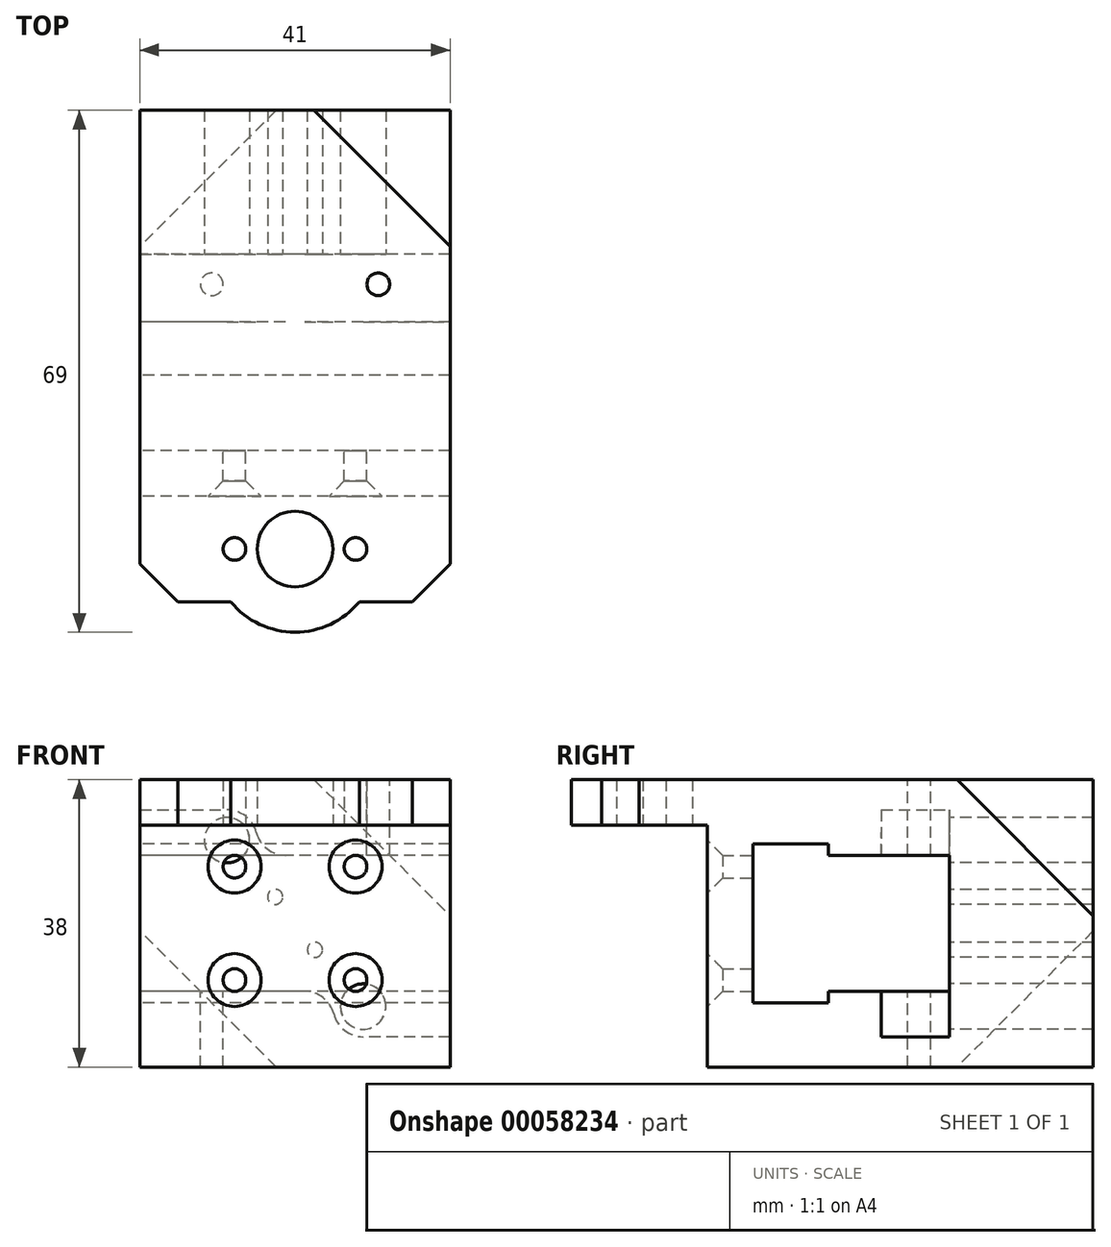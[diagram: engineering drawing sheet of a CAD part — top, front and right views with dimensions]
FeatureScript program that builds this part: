
annotation { "Feature Type Name" : "Feature", "Feature Type Description" : "" }
export const myFeature = defineFeature(function(context is Context, id is Id, definition is map)
    precondition{}
    {
        {
            var Q0;
            Q0=qCreatedBy(makeId("Right.planeOp"),FACE);
            var sketch = newSketch(context, id + "F0", { "sketchPlane" : qUnion([Q0])});
            skLineSegment(sketch, "E0", {"start": v(0, 0) * mm, "end": v(22, 0) * mm, "construction": true});
            skLineSegment(sketch, "E1", {"start": v(22, 0) * mm, "end": v(22, 31.5) * mm, "construction": true});
            skLineSegment(sketch, "E2", {"start": v(0, 10.5) * mm, "end": v(10, 10.5) * mm});
            skLineSegment(sketch, "E3", {"start": v(10, 10.5) * mm, "end": v(10, 9) * mm});
            skLineSegment(sketch, "E4", {"start": v(10, 9) * mm, "end": v(26, 9) * mm});
            skLineSegment(sketch, "E5.MirrorCS", {"start": v(0, -10.5) * mm, "end": v(10, -10.5) * mm});
            skLineSegment(sketch, "E6.MirrorCS", {"start": v(10, -10.5) * mm, "end": v(10, -9) * mm});
            skLineSegment(sketch, "E7.MirrorCS", {"start": v(10, -9) * mm, "end": v(26, -9) * mm});
            skLineSegment(sketch, "E8", {"start": v(0, 10.5) * mm, "end": v(0, -10.5) * mm});
            skLineSegment(sketch, "E9", {"start": v(26, 9) * mm, "end": v(26, 19) * mm});
            skLineSegment(sketch, "E10", {"start": v(26, 19) * mm, "end": v(-20, 19) * mm});
            skLineSegment(sketch, "E11", {"start": v(-20, 19) * mm, "end": v(-20, 13) * mm});
            skLineSegment(sketch, "E12", {"start": v(-20, 13) * mm, "end": v(-6, 13) * mm});
            skLineSegment(sketch, "E13", {"start": v(-6, 13) * mm, "end": v(-6, -19) * mm});
            skLineSegment(sketch, "E14.MirrorCS", {"start": v(26, -9) * mm, "end": v(26, -19) * mm});
            skLineSegment(sketch, "E15", {"start": v(26, -19) * mm, "end": v(-6, -19) * mm});
            skSolve(sketch);
        }
        {
            var Q0;
            Q0 = qSketchRegion(id + "F0", true);
            extrude(context, id + "F1", {"entities" : qUnion([Q0]), "depth" : 41 * mm, "symmetric" : true});
        }
        {
            var Q0;
            Q0=makeQuery(id+"F1.opExtrude","SWEPT_FACE",FACE,{"disambiguationData":[OSD([sQuery(id+"F0.wireOp",EDGE,"E12")])]});
            var sketch = newSketch(context, id + "F2", { "sketchPlane" : qUnion([Q0])});
            skLineSegment(sketch, "E16", {"start": v(-20.5, 13) * mm, "end": v(20.5, 13) * mm, "construction": true});
            skLineSegment(sketch, "E17", {"start": v(0, 13) * mm, "end": v(0, 20) * mm, "construction": true});
            skCircle(sketch, "E18", {"center": v(-8, 13) * mm, "radius": 1.5 * mm});
            skCircle(sketch, "E19.MirrorC", {"center": v(8, 13) * mm, "radius": 1.5 * mm});
            skCircle(sketch, "E20", {"center": v(0, 13) * mm, "radius": 5 * mm});
            skSolve(sketch);
        }
        {
            var Q0;
            Q0 = qSketchRegion(id + "F2", true);
            extrude(context, id + "F3", {"entities" : qUnion([Q0]), "operationType" : NewBodyOperationType.REMOVE, "endBound" : BoundingType.THROUGH_ALL, "oppositeDirection" : true, "depth" : 25 * mm});
        }
        {
            var Q0;
            Q0=makeQuery(id+"F1.opExtrude","SWEPT_FACE",FACE,{"disambiguationData":[OSD([sQuery(id+"F0.wireOp",EDGE,"E10")])]});
            var sketch = newSketch(context, id + "F4", { "sketchPlane" : qUnion([Q0])});
            skArc(sketch, "E21", {"start": v(8.49, -20) * mm, "mid": v(0, -24) * mm, "end": v(-8.49, -20) * mm});
            skLineSegment(sketch, "E22", {"start": v(8.49, -20) * mm, "end": v(-8.49, -20) * mm});
            skSolve(sketch);
        }
        {
            var Q0;
            Q0 = qSketchRegion(id + "F4", true);
            var Q1;
            Q1=makeQuery(id+"F1.opExtrude","SWEPT_FACE",FACE,{"disambiguationData":[OSD([sQuery(id+"F0.wireOp",EDGE,"E12")])]});
            extrude(context, id + "F5", {"entities" : qUnion([Q0]), "operationType" : NewBodyOperationType.ADD, "endBound" : BoundingType.UP_TO_SURFACE, "oppositeDirection" : true, "endBoundEntityFace" : qUnion([Q1]), "depth" : 25 * mm});
        }
        {
            var Q0;
            Q0=makeQuery(id+"F1.opExtrude","SWEPT_FACE",FACE,{"disambiguationData":[OSD([sQuery(id+"F0.wireOp",EDGE,"E8")])]});
            var sketch = newSketch(context, id + "F6", { "sketchPlane" : qUnion([Q0])});
            skLineSegment(sketch, "E23", {"start": v(-20.5, 0) * mm, "end": v(0, 0) * mm, "construction": true});
            skLineSegment(sketch, "E24", {"start": v(0, 0) * mm, "end": v(0, 10.5) * mm, "construction": true});
            skCircle(sketch, "E25", {"center": v(-8, 7.5) * mm, "radius": 1.5 * mm});
            skCircle(sketch, "E26.MirrorC", {"center": v(8, 7.5) * mm, "radius": 1.5 * mm});
            skCircle(sketch, "E27.MirrorC", {"center": v(8, -7.5) * mm, "radius": 1.5 * mm});
            skCircle(sketch, "E28.MirrorC", {"center": v(-8, -7.5) * mm, "radius": 1.5 * mm});
            skSolve(sketch);
        }
        {
            var Q0;
            Q0 = qSketchRegion(id + "F6", true);
            extrude(context, id + "F7", {"entities" : qUnion([Q0]), "operationType" : NewBodyOperationType.REMOVE, "endBound" : BoundingType.THROUGH_ALL, "oppositeDirection" : true, "depth" : 25 * mm});
        }
        {
            var Q0;
            Q0=makeQuery(id+"F7.boolean.opBoolean","INTERSECT",EDGE,{"derivedFrom":[makeQuery(id+"F1.opExtrude","SWEPT_FACE",FACE,{"disambiguationData":[OSD([sQuery(id+"F0.wireOp",EDGE,"E13")])]}),makeQuery(id+"F7.opExtrude","SWEPT_FACE",FACE,{"disambiguationData":[OSD([sQuery(id+"F6.wireOp",EDGE,"E26.MirrorC")])]})]});
            var Q1;
            Q1=makeQuery(id+"F7.boolean.opBoolean","INTERSECT",EDGE,{"derivedFrom":[makeQuery(id+"F1.opExtrude","SWEPT_FACE",FACE,{"disambiguationData":[OSD([sQuery(id+"F0.wireOp",EDGE,"E13")])]}),makeQuery(id+"F7.opExtrude","SWEPT_FACE",FACE,{"disambiguationData":[OSD([sQuery(id+"F6.wireOp",EDGE,"E25")])]})]});
            var Q2;
            Q2=makeQuery(id+"F7.boolean.opBoolean","INTERSECT",EDGE,{"derivedFrom":[makeQuery(id+"F1.opExtrude","SWEPT_FACE",FACE,{"disambiguationData":[OSD([sQuery(id+"F0.wireOp",EDGE,"E13")])]}),makeQuery(id+"F7.opExtrude","SWEPT_FACE",FACE,{"disambiguationData":[OSD([sQuery(id+"F6.wireOp",EDGE,"E28.MirrorC")])]})]});
            var Q3;
            Q3=makeQuery(id+"F7.boolean.opBoolean","INTERSECT",EDGE,{"derivedFrom":[makeQuery(id+"F1.opExtrude","SWEPT_FACE",FACE,{"disambiguationData":[OSD([sQuery(id+"F0.wireOp",EDGE,"E13")])]}),makeQuery(id+"F7.opExtrude","SWEPT_FACE",FACE,{"disambiguationData":[OSD([sQuery(id+"F6.wireOp",EDGE,"E27.MirrorC")])]})]});
            chamfer(context, id + "F8", {"entities" : qUnion([Q0, Q1, Q2, Q3]), "width" : 2 * mm, "tangentPropagation" : true});
        }
        {
            var Q0;
            Q0=makeQuery(id+"F5.boolean.opBoolean","MERGE",FACE,{"derivedFrom":[makeQuery(id+"F1.opExtrude","SWEPT_FACE",FACE,{"disambiguationData":[OSD([sQuery(id+"F0.wireOp",EDGE,"E10")])]}),makeQuery(id+"F5.opExtrude","CAP_FACE",FACE,{"disambiguationData":[OSD([sQuery(id+"F4.wireOp",EDGE,"E21"),sQuery(id+"F4.wireOp",EDGE,"E22")])],"isStart":true})]});
            var sketch = newSketch(context, id + "F9", { "sketchPlane" : qUnion([Q0])});
            skLineSegment(sketch, "E29", {"start": v(20.5, 22) * mm, "end": v(-20.5, 22) * mm, "construction": true});
            skLineSegment(sketch, "E30", {"start": v(0, 22) * mm, "end": v(0, 0) * mm, "construction": true});
            skCircle(sketch, "E31", {"center": v(-11, 22) * mm, "radius": 1.5 * mm});
            skCircle(sketch, "E32.MirrorC", {"center": v(11, 22) * mm, "radius": 1.5 * mm});
            skSolve(sketch);
        }
        {
            var Q0;
            Q0 = qSketchRegion(id + "F9", true);
            extrude(context, id + "F10", {"entities" : qUnion([Q0]), "operationType" : NewBodyOperationType.REMOVE, "endBound" : BoundingType.THROUGH_ALL, "oppositeDirection" : true, "depth" : 25 * mm});
        }
        {
            var Q0;
            Q0=makeQuery(id+"F1.opExtrude","SWEPT_FACE",FACE,{"disambiguationData":[OSD([sQuery(id+"F0.wireOp",EDGE,"E9")])]});
            var sketch = newSketch(context, id + "F11", { "sketchPlane" : qUnion([Q0])});
            skLineSegment(sketch, "E33.0", {"start": v(9.5, 19) * mm, "end": v(12.5, 19) * mm, "construction": true});
            skLineSegment(sketch, "E34", {"start": v(11, 11) * mm, "end": v(11, 19) * mm, "construction": true});
            skCircle(sketch, "E35", {"center": v(2.63, 3.5) * mm, "radius": 1 * mm});
            skLineSegment(sketch, "E36", {"start": v(11, 11) * mm, "end": v(9, 11) * mm, "construction": true});
            skCircle(sketch, "E37", {"center": v(9, 11) * mm, "radius": 2 * mm, "construction": true});
            skCircle(sketch, "E38", {"center": v(9, 11) * mm, "radius": 3 * mm});
            skLineSegment(sketch, "E39", {"start": v(0, 9) * mm, "end": v(0, 0) * mm, "construction": true});
            skLineSegment(sketch, "E40", {"start": v(0, 0) * mm, "end": v(-37.44, 0) * mm, "construction": true});
            skLineSegment(sketch, "E41.bottom", {"start": v(-20.5, 19) * mm, "end": v(20.5, 19) * mm});
            skLineSegment(sketch, "E41.top", {"start": v(-20.5, -19) * mm, "end": v(20.5, -19) * mm});
            skLineSegment(sketch, "E41.left", {"start": v(-20.5, 19) * mm, "end": v(-20.5, -19) * mm});
            skLineSegment(sketch, "E41.right", {"start": v(20.5, 19) * mm, "end": v(20.5, -19) * mm});
            skCircle(sketch, "E42.MirrorC", {"center": v(-2.63, 3.5) * mm, "radius": 1 * mm, "construction": true});
            skCircle(sketch, "E43.MirrorC", {"center": v(-9, 11) * mm, "radius": 3 * mm, "construction": true});
            skCircle(sketch, "E44.MirrorC", {"center": v(-2.63, -3.5) * mm, "radius": 1 * mm});
            skCircle(sketch, "E45.MirrorC", {"center": v(-9, -11) * mm, "radius": 3 * mm});
            skSolve(sketch);
        }
        {
            var Q0;
            Q0 = qSketchRegion(id + "F11", true);
            extrude(context, id + "F12", {"entities" : qUnion([Q0]), "operationType" : NewBodyOperationType.ADD, "depth" : 19 * mm});
        }
        {
            var Q0;
            Q0=makeQuery(id+"F12.opExtrude","CAP_FACE",FACE,{"disambiguationData":[OSD([sQuery(id+"F11.wireOp",EDGE,"E35"),sQuery(id+"F11.wireOp",EDGE,"E38"),sQuery(id+"F11.wireOp",EDGE,"E41.bottom"),sQuery(id+"F11.wireOp",EDGE,"E41.top"),sQuery(id+"F11.wireOp",EDGE,"E41.left"),sQuery(id+"F11.wireOp",EDGE,"E41.right"),sQuery(id+"F11.wireOp",EDGE,"E44.MirrorC"),sQuery(id+"F11.wireOp",EDGE,"E45.MirrorC")])],"isStart":false});
            var sketch = newSketch(context, id + "F13", { "sketchPlane" : qUnion([Q0])});
            skCircle(sketch, "E46.0", {"center": v(9, 11) * mm, "radius": 3 * mm});
            skCircle(sketch, "E46.1", {"center": v(-9, -11) * mm, "radius": 3 * mm});
            skSolve(sketch);
        }
        {
            var Q0;
            Q0 = qSketchRegion(id + "F13", true);
            var Q1;
            Q1=makeQuery(id+"F10.boolean.opBoolean","COPY",FACE,{"disambiguationData":[TD([makeQuery(id+"F1.opExtrude","SWEPT_FACE",FACE,{"disambiguationData":[OSD([sQuery(id+"F0.wireOp",EDGE,"E4")])]})])],"derivedFrom":makeQuery(id+"F10.opExtrude","SWEPT_FACE",FACE,{"disambiguationData":[OSD([sQuery(id+"F9.wireOp",EDGE,"E31")])]})});
            extrude(context, id + "F14", {"entities" : qUnion([Q0]), "operationType" : NewBodyOperationType.REMOVE, "oppositeDirection" : true, "endBoundEntityFace" : qUnion([Q1]), "depth" : 28 * mm});
        }
        {
            var Q0;
            Q0=makeQuery(id+"F14.boolean.opBoolean","COPY",FACE,{"derivedFrom":makeQuery(id+"F14.opExtrude","CAP_FACE",FACE,{"disambiguationData":[OSD([sQuery(id+"F13.wireOp",EDGE,"E46.0")])],"isStart":false})});
            var sketch = newSketch(context, id + "F15", { "sketchPlane" : qUnion([Q0])});
            skArc(sketch, "E47.0", {"start": v(11.24, 9) * mm, "mid": v(9, 14) * mm, "end": v(6.76, 9) * mm});
            skLineSegment(sketch, "E48.0", {"start": v(20.5, -19) * mm, "end": v(20.5, 19) * mm, "construction": true});
            skLineSegment(sketch, "E49", {"start": v(11.24, 9) * mm, "end": v(20.5, 9) * mm});
            skLineSegment(sketch, "E50", {"start": v(20.5, 9) * mm, "end": v(20.5, 19) * mm});
            skLineSegment(sketch, "E51", {"start": v(20.5, 19) * mm, "end": v(0, 19) * mm});
            skLineSegment(sketch, "E52", {"start": v(0, 19) * mm, "end": v(0, 9) * mm});
            skLineSegment(sketch, "E53", {"start": v(0, 9) * mm, "end": v(6.76, 9) * mm});
            skArc(sketch, "E54.0", {"start": v(-11.24, -9) * mm, "mid": v(-9, -14) * mm, "end": v(-6.76, -9) * mm});
            skLineSegment(sketch, "E55", {"start": v(-11.24, -9) * mm, "end": v(-20.5, -9) * mm});
            skLineSegment(sketch, "E56.0", {"start": v(-20.5, -19) * mm, "end": v(-20.5, 19) * mm, "construction": true});
            skLineSegment(sketch, "E57", {"start": v(-20.5, -9) * mm, "end": v(-20.5, -19) * mm});
            skLineSegment(sketch, "E58", {"start": v(-20.5, -19) * mm, "end": v(0, -19) * mm});
            skLineSegment(sketch, "E59", {"start": v(0, -19) * mm, "end": v(0, -9) * mm});
            skLineSegment(sketch, "E60", {"start": v(0, -9) * mm, "end": v(-6.76, -9) * mm});
            skSolve(sketch);
        }
        {
            var Q0;
            Q0 = qSketchRegion(id + "F15", true);
            var Q1;
            Q1=makeQuery(id+"F12.opExtrude","CAP_FACE",FACE,{"disambiguationData":[OSD([sQuery(id+"F11.wireOp",EDGE,"E35"),sQuery(id+"F11.wireOp",EDGE,"E38"),sQuery(id+"F11.wireOp",EDGE,"E41.bottom"),sQuery(id+"F11.wireOp",EDGE,"E41.top"),sQuery(id+"F11.wireOp",EDGE,"E41.left"),sQuery(id+"F11.wireOp",EDGE,"E41.right"),sQuery(id+"F11.wireOp",EDGE,"E44.MirrorC"),sQuery(id+"F11.wireOp",EDGE,"E45.MirrorC")])],"isStart":false});
            extrude(context, id + "F16", {"entities" : qUnion([Q0]), "operationType" : NewBodyOperationType.ADD, "endBound" : BoundingType.UP_TO_SURFACE, "endBoundEntityFace" : qUnion([Q1]), "depth" : 25 * mm});
        }
        {
            var Q0;
            Q0=makeQuery(id+"F14.boolean.opBoolean","COPY",FACE,{"derivedFrom":makeQuery(id+"F14.opExtrude","CAP_FACE",FACE,{"disambiguationData":[OSD([sQuery(id+"F13.wireOp",EDGE,"E46.0")])],"isStart":false})});
            var sketch = newSketch(context, id + "F17", { "sketchPlane" : qUnion([Q0])});
            skCircle(sketch, "E61", {"center": v(9, 11) * mm, "radius": 4 * mm});
            skCircle(sketch, "E62", {"center": v(-9, -11) * mm, "radius": 4 * mm});
            skSolve(sketch);
        }
        {
            var Q0;
            Q0 = qSketchRegion(id + "F17", true);
            var Q1;
            Q1=makeQuery(id+"F12.opExtrude","CAP_FACE",FACE,{"disambiguationData":[OSD([sQuery(id+"F11.wireOp",EDGE,"E35"),sQuery(id+"F11.wireOp",EDGE,"E38"),sQuery(id+"F11.wireOp",EDGE,"E41.bottom"),sQuery(id+"F11.wireOp",EDGE,"E41.top"),sQuery(id+"F11.wireOp",EDGE,"E41.left"),sQuery(id+"F11.wireOp",EDGE,"E41.right"),sQuery(id+"F11.wireOp",EDGE,"E44.MirrorC"),sQuery(id+"F11.wireOp",EDGE,"E45.MirrorC")])],"isStart":true});
            extrude(context, id + "F18", {"entities" : qUnion([Q0]), "operationType" : NewBodyOperationType.REMOVE, "endBound" : BoundingType.UP_TO_SURFACE, "endBoundEntityFace" : qUnion([Q1]), "depth" : 25 * mm});
        }
        {
            var Q0;
            Q0=makeQuery(id+"F12.opExtrude","CAP_FACE",FACE,{"disambiguationData":[OSD([sQuery(id+"F11.wireOp",EDGE,"E35"),sQuery(id+"F11.wireOp",EDGE,"E38"),sQuery(id+"F11.wireOp",EDGE,"E41.bottom"),sQuery(id+"F11.wireOp",EDGE,"E41.top"),sQuery(id+"F11.wireOp",EDGE,"E41.left"),sQuery(id+"F11.wireOp",EDGE,"E41.right"),sQuery(id+"F11.wireOp",EDGE,"E44.MirrorC"),sQuery(id+"F11.wireOp",EDGE,"E45.MirrorC")])],"isStart":false});
            var sketch = newSketch(context, id + "F19", { "sketchPlane" : qUnion([Q0])});
            skLineSegment(sketch, "E63.bottom", {"start": v(-20.5, 19) * mm, "end": v(-2.5, 19) * mm});
            skLineSegment(sketch, "E63.top", {"start": v(-20.5, 1) * mm, "end": v(-2.5, 1) * mm});
            skLineSegment(sketch, "E63.left", {"start": v(-20.5, 19) * mm, "end": v(-20.5, 1) * mm});
            skLineSegment(sketch, "E63.right", {"start": v(-2.5, 19) * mm, "end": v(-2.5, 1) * mm});
            skLineSegment(sketch, "E64.bottom", {"start": v(20.5, -19) * mm, "end": v(2.5, -19) * mm});
            skLineSegment(sketch, "E64.top", {"start": v(20.5, -1) * mm, "end": v(2.5, -1) * mm});
            skLineSegment(sketch, "E64.left", {"start": v(20.5, -19) * mm, "end": v(20.5, -1) * mm});
            skLineSegment(sketch, "E64.right", {"start": v(2.5, -19) * mm, "end": v(2.5, -1) * mm});
            skSolve(sketch);
        }
        {
            var Q0;
            Q0 = qSketchRegion(id + "F19", true);
            extrude(context, id + "F20", {"entities" : qUnion([Q0]), "operationType" : NewBodyOperationType.REMOVE, "oppositeDirection" : true, "depth" : 18 * mm});
        }
        {
            var Q0;
            Q0=makeQuery(id+"F20.boolean.opBoolean","COPY",EDGE,{"derivedFrom":makeQuery(id+"F20.opExtrude","CAP_EDGE",EDGE,{"disambiguationData":[OSD([sQuery(id+"F19.wireOp",EDGE,"E63.right")])],"isStart":false})});
            var Q1;
            Q1=makeQuery(id+"F20.boolean.opBoolean","COPY",EDGE,{"derivedFrom":makeQuery(id+"F20.opExtrude","CAP_EDGE",EDGE,{"disambiguationData":[OSD([sQuery(id+"F19.wireOp",EDGE,"E64.right")])],"isStart":false})});
            var Q2;
            Q2=makeQuery(id+"F20.boolean.opBoolean","COPY",EDGE,{"derivedFrom":makeQuery(id+"F20.opExtrude","CAP_EDGE",EDGE,{"disambiguationData":[OSD([sQuery(id+"F19.wireOp",EDGE,"E63.top")])],"isStart":false})});
            var Q3;
            Q3=makeQuery(id+"F20.boolean.opBoolean","COPY",EDGE,{"derivedFrom":makeQuery(id+"F20.opExtrude","SWEPT_EDGE",EDGE,{"disambiguationData":[OSD([sQuery(id+"F19.wireOp",EDGE,"E63.top"),sQuery(id+"F19.wireOp",EDGE,"E63.right")])]})});
            var Q4;
            Q4=makeQuery(id+"F20.boolean.opBoolean","COPY",EDGE,{"derivedFrom":makeQuery(id+"F20.opExtrude","SWEPT_EDGE",EDGE,{"disambiguationData":[OSD([sQuery(id+"F19.wireOp",EDGE,"E64.top"),sQuery(id+"F19.wireOp",EDGE,"E64.right")])]})});
            var Q5;
            Q5=makeQuery(id+"F20.boolean.opBoolean","COPY",EDGE,{"derivedFrom":makeQuery(id+"F20.opExtrude","CAP_EDGE",EDGE,{"disambiguationData":[OSD([sQuery(id+"F19.wireOp",EDGE,"E64.top")])],"isStart":false})});
            chamfer(context, id + "F21", {"entities" : qUnion([Q0, Q1, Q2, Q3, Q4, Q5]), "width" : 18 * mm, "tangentPropagation" : true});
        }
        {
            var Q0;
            Q0=makeQuery(id+"F1.opExtrude","CAP_EDGE",EDGE,{"disambiguationData":[OSD([sQuery(id+"F0.wireOp",EDGE,"E11")])],"isStart":false});
            var Q1;
            Q1=makeQuery(id+"F1.opExtrude","CAP_EDGE",EDGE,{"disambiguationData":[OSD([sQuery(id+"F0.wireOp",EDGE,"E11")])],"isStart":true});
            chamfer(context, id + "F22", {"entities" : qUnion([Q0, Q1]), "width" : 5 * mm, "tangentPropagation" : true});
        }
        {
            var Q0;
            {var subQ0=sQuery(id+"F11.wireOp",EDGE,"E45.MirrorC");var subQ1=sQuery(id+"F11.wireOp",EDGE,"E44.MirrorC");var subQ2=sQuery(id+"F11.wireOp",EDGE,"E41.right");var subQ3=sQuery(id+"F11.wireOp",EDGE,"E41.left");var subQ4=sQuery(id+"F11.wireOp",EDGE,"E41.top");var subQ5=sQuery(id+"F11.wireOp",EDGE,"E41.bottom");var subQ6=sQuery(id+"F11.wireOp",EDGE,"E38");var subQ7=sQuery(id+"F11.wireOp",EDGE,"E35");Q0=makeQuery(id+"F18.boolean.opBoolean","MERGE",FACE,{"derivedFrom":[makeQuery(id+"F12.opExtrude","CAP_FACE",FACE,{"disambiguationData":[OSD([subQ7,subQ6,subQ5,subQ4,subQ3,subQ2,subQ1,subQ0])],"isStart":true}),makeQuery(id+"F18.opExtrude","CAP_FACE",FACE,{"disambiguationData":[OSD([subQ7,subQ6,subQ5,subQ4,subQ3,subQ2,subQ1,subQ0]),ownerDisambiguation([makeQuery(id+"F17.imprint","IMPRINT",EDGE,{"derivedFrom":sQuery(id+"F17.wireOp",EDGE,"E61")})])],"isStart":false}),makeQuery(id+"F18.opExtrude","CAP_FACE",FACE,{"disambiguationData":[OSD([subQ7,subQ6,subQ5,subQ4,subQ3,subQ2,subQ1,subQ0]),ownerDisambiguation([makeQuery(id+"F17.imprint","IMPRINT",EDGE,{"derivedFrom":sQuery(id+"F17.wireOp",EDGE,"E62")})])],"isStart":false})]});}
            var sketch = newSketch(context, id + "F23", { "sketchPlane" : qUnion([Q0])});
            skArc(sketch, "E65.0", {"start": v(12.46, -9) * mm, "mid": v(12.46, -13) * mm, "end": v(9, -15) * mm});
            skLineSegment(sketch, "E65.1", {"start": v(20.5, -9) * mm, "end": v(12.46, -9) * mm});
            skLineSegment(sketch, "E66", {"start": v(20.5, -9) * mm, "end": v(20.5, -15) * mm});
            skLineSegment(sketch, "E67", {"start": v(20.5, -15) * mm, "end": v(9, -15) * mm});
            skPoint(sketch, "E67.endSnap0", {"position": v(9, -15) * mm});
            skPoint(sketch, "E68.orphan", {"position": v(5.54, -9) * mm});
            skArc(sketch, "E69.0", {"start": v(-12.46, 9) * mm, "mid": v(-12.46, 13) * mm, "end": v(-9, 15) * mm});
            skLineSegment(sketch, "E69.1", {"start": v(-12.46, 9) * mm, "end": v(-20.5, 9) * mm});
            skLineSegment(sketch, "E70", {"start": v(-20.5, 9) * mm, "end": v(-20.5, 15) * mm});
            skLineSegment(sketch, "E71", {"start": v(-20.5, 15) * mm, "end": v(-9, 15) * mm});
            skPoint(sketch, "E72.orphan", {"position": v(-5.54, 9) * mm});
            skSolve(sketch);
        }
        {
            var Q0;
            Q0 = qSketchRegion(id + "F23", true);
            var Q1;
            Q1=makeQuery(id+"F18.boolean.opBoolean","MERGE",FACE,{"derivedFrom":[makeQuery(id+"F14.boolean.opBoolean","COPY",FACE,{"derivedFrom":makeQuery(id+"F14.opExtrude","CAP_FACE",FACE,{"disambiguationData":[OSD([sQuery(id+"F13.wireOp",EDGE,"E46.1")])],"isStart":false})}),makeQuery(id+"F18.opExtrude","CAP_FACE",FACE,{"disambiguationData":[OSD([sQuery(id+"F17.wireOp",EDGE,"E62")])],"isStart":true})]});
            extrude(context, id + "F24", {"entities" : qUnion([Q0]), "operationType" : NewBodyOperationType.REMOVE, "endBound" : BoundingType.UP_TO_SURFACE, "endBoundEntityFace" : qUnion([Q1]), "depth" : 25 * mm});
        }
        {
            var Q0;
            Q0=makeQuery(id+"F18.boolean.opBoolean","INTERSECT",EDGE,{"disambiguationData":[OD(1.0)],"derivedFrom":[makeQuery(id+"F16.boolean.opBoolean","MERGE",FACE,{"derivedFrom":[makeQuery(id+"F1.opExtrude","SWEPT_FACE",FACE,{"disambiguationData":[OSD([sQuery(id+"F0.wireOp",EDGE,"E4")])]}),makeQuery(id+"F16.opExtrude","SWEPT_FACE",FACE,{"disambiguationData":[OSD([sQuery(id+"F15.wireOp",EDGE,"E49")])]})]}),makeQuery(id+"F18.opExtrude","SWEPT_FACE",FACE,{"disambiguationData":[OSD([sQuery(id+"F17.wireOp",EDGE,"E61")])]})]});
            var Q1;
            Q1=makeQuery(id+"F18.boolean.opBoolean","INTERSECT",EDGE,{"disambiguationData":[OD(1.0)],"derivedFrom":[makeQuery(id+"F16.boolean.opBoolean","MERGE",FACE,{"derivedFrom":[makeQuery(id+"F1.opExtrude","SWEPT_FACE",FACE,{"disambiguationData":[OSD([sQuery(id+"F0.wireOp",EDGE,"E7.MirrorCS")])]}),makeQuery(id+"F16.opExtrude","SWEPT_FACE",FACE,{"disambiguationData":[OSD([sQuery(id+"F15.wireOp",EDGE,"E55")])]})]}),makeQuery(id+"F18.opExtrude","SWEPT_FACE",FACE,{"disambiguationData":[OSD([sQuery(id+"F17.wireOp",EDGE,"E62")])]})]});
            fillet(context, id + "F25", {"entities" : qUnion([Q0, Q1]), "radius" : 4 * mm, "tangentPropagation" : true, "allowEdgeOverflow" : false});
        }
    });
